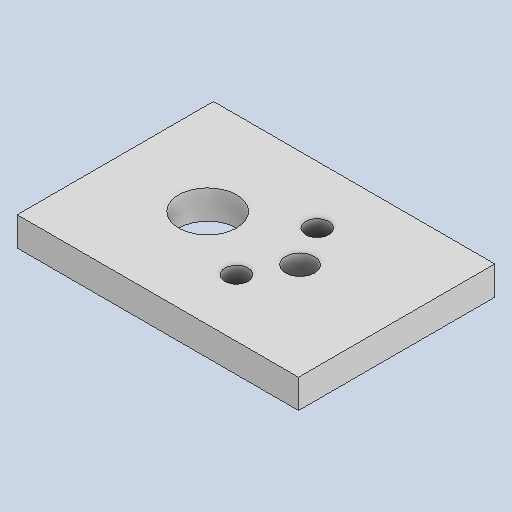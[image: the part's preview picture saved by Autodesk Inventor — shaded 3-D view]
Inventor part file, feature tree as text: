
AUTODESK INVENTOR PART (.ipt)
format: ipt  version: 2025.1 (Build 291241020, 241B)  size: 140,800 bytes
history: native  units: in
note: dims shown in document units (in); Inventor stores cm internally (conversion verified against a paired STEP export)
features: hole x4, sketch x3, extrude x1
ambient origin geometry x8: Origin, YZ Plane, XZ Plane, XY Plane, X Axis, Y Axis, Z Axis, Center Point
bodies: Solid1 (feature_tree)
feature tree (8):
  extrude  "Extrusion1"  Depth=1.7in
  sketch  "Sketch2"  dims[d2=0.25in d3=0.0in d10=0.8375in]
  hole  "Hole1"  [1 undecoded]
  hole  "Hole2"  [1 undecoded]
  hole  "Hole3"  [1 undecoded]
  hole  "Hole4"  [1 undecoded]
  sketch  "Sketch1"  dims[d0=2.4375in d1=1.7in]
  sketch  "Sketch3"  dims[d11=0.85in d14=0.85in d15=0.8in d18=0.5in d19=0.5in d20=0.6in d21=0.6in d22=0.25in d23=0.75in d24=0.375in d25=0.25in d26=0.5635in d27=0.432in d28=0.8108in d29=0.5in d30=0.75in d31=0.375in d32=0.25in d33=0.5635in d34=1.0in d35=0.8108in d36=0.201in d37=0.75in d38=0.385in d39=0.25in d40=0.5635in d41=1.0in d42=0.8108in d43=0.104in d44=0.276in d45=0.375in d46=0.25in d47=0.5635in d48=0.432in d49=0.8108in d50=0.25in d51=0.25in d52=0.125in d53=1.0in d54=1.0in d55=1.0in d56=0.15in d57=0.25in d58=0.375in d59=0.5635in d60=0.75in d61=0.8108in d62=0.0625in d63=0.75in d64=0.375in]
note: 4 required parameter values undecoded (feature->parameter linkage not recoverable at this tier; creation-order binding heuristic only, values carry confidence <= 0.55)
